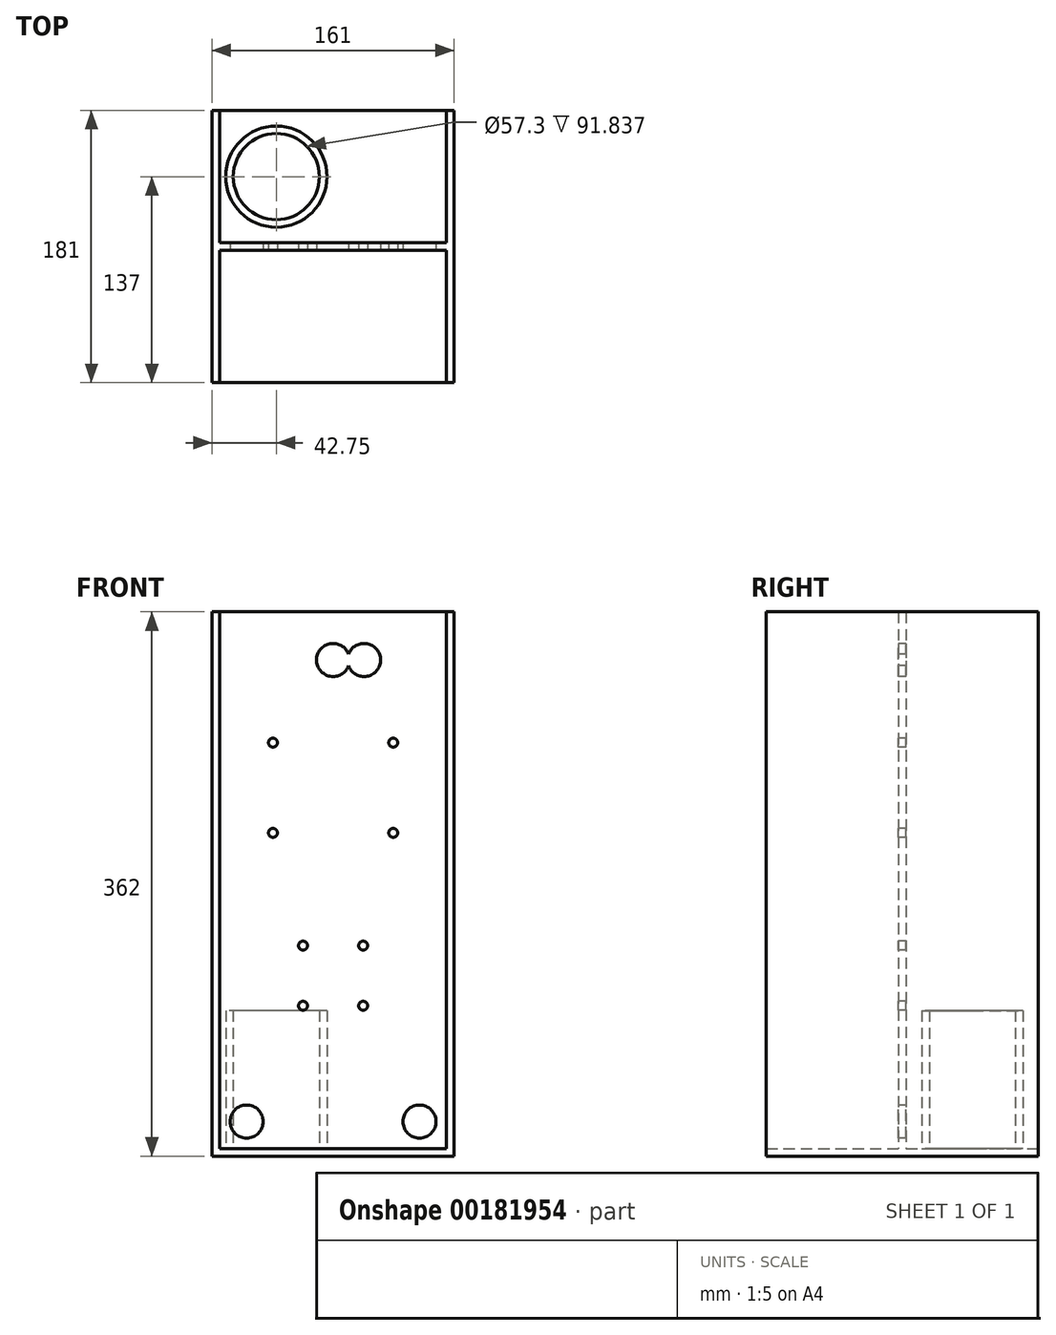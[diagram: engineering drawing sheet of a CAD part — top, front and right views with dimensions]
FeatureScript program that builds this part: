
annotation { "Feature Type Name" : "Feature", "Feature Type Description" : "" }
export const myFeature = defineFeature(function(context is Context, id is Id, definition is map)
    precondition{}
    {
        {
            var Q0;
            Q0=qCreatedBy(makeId("Top.planeOp"),FACE);
            var sketch = newSketch(context, id + "F0", { "sketchPlane" : qUnion([Q0])});
            skLineSegment(sketch, "E0.bottom", {"start": v(80.5, -90.5) * mm, "end": v(-80.5, -90.5) * mm});
            skLineSegment(sketch, "E0.top", {"start": v(80.5, 90.5) * mm, "end": v(-80.5, 90.5) * mm});
            skLineSegment(sketch, "E0.left", {"start": v(80.5, -90.5) * mm, "end": v(80.5, 90.5) * mm});
            skLineSegment(sketch, "E0.right", {"start": v(-80.5, -90.5) * mm, "end": v(-80.5, 90.5) * mm});
            skPoint(sketch, "E0.middle", {"position": v(0, 0) * mm});
            skSolve(sketch);
        }
        {
            var Q0;
            Q0 = qSketchRegion(id + "F0", true);
            extrude(context, id + "F1", {"entities" : qUnion([Q0]), "depth" : 5 * mm});
        }
        {
            var Q0;
            Q0=makeQuery(id+"F1.opExtrude","CAP_FACE",FACE,{"disambiguationData":[OSD([sQuery(id+"F0.wireOp",EDGE,"E0.bottom"),sQuery(id+"F0.wireOp",EDGE,"E0.top"),sQuery(id+"F0.wireOp",EDGE,"E0.left"),sQuery(id+"F0.wireOp",EDGE,"E0.right")])],"isStart":false});
            var sketch = newSketch(context, id + "F2", { "sketchPlane" : qUnion([Q0])});
            skLineSegment(sketch, "E1.0", {"start": v(-80.5, -90.5) * mm, "end": v(-80.5, 90.5) * mm});
            skLineSegment(sketch, "E2.0", {"start": v(80.5, -90.5) * mm, "end": v(80.5, 90.5) * mm});
            skLineSegment(sketch, "E3.0", {"start": v(80.5, 90.5) * mm, "end": v(75.5, 90.5) * mm});
            skLineSegment(sketch, "E4.0", {"start": v(80.5, -90.5) * mm, "end": v(75.5, -90.5) * mm});
            skLineSegment(sketch, "E5.0", {"start": v(-75.5, -90.5) * mm, "end": v(-75.5, 90.5) * mm});
            skLineSegment(sketch, "E6.0", {"start": v(75.5, -90.5) * mm, "end": v(75.5, 90.5) * mm});
            skLineSegment(sketch, "E7.trimOffspring", {"start": v(-75.5, 90.5) * mm, "end": v(-80.5, 90.5) * mm});
            skLineSegment(sketch, "E8.trimOffspring", {"start": v(-75.5, -90.5) * mm, "end": v(-80.5, -90.5) * mm});
            skLineSegment(sketch, "E9.bottom", {"start": v(75.5, 2.5) * mm, "end": v(-75.5, 2.5) * mm});
            skLineSegment(sketch, "E9.top", {"start": v(75.5, -2.5) * mm, "end": v(-75.5, -2.5) * mm});
            skLineSegment(sketch, "E9.left", {"start": v(75.5, 2.5) * mm, "end": v(75.5, -2.5) * mm});
            skLineSegment(sketch, "E9.right", {"start": v(-75.5, 2.5) * mm, "end": v(-75.5, -2.5) * mm});
            skPoint(sketch, "E9.middle", {"position": v(0, 0) * mm});
            skSolve(sketch);
        }
        {
            var Q0;
            Q0 = qSketchRegion(id + "F2", true);
            extrude(context, id + "F3", {"entities" : qUnion([Q0]), "operationType" : NewBodyOperationType.ADD, "depth" : 357 * mm});
        }
        {
            var Q0;
            Q0=qCreatedBy(makeId("Front.planeOp"),FACE);
            var sketch = newSketch(context, id + "F4", { "sketchPlane" : qUnion([Q0])});
            skLineSegment(sketch, "E10.0", {"start": v(-75.5, 362) * mm, "end": v(-75.5, 5) * mm});
            skLineSegment(sketch, "E11.0", {"start": v(75.5, 362) * mm, "end": v(75.5, 5) * mm});
            skLineSegment(sketch, "E12.0", {"start": v(75.5, 5) * mm, "end": v(-75.5, 5) * mm});
            skLineSegment(sketch, "E13.0", {"start": v(57.5, 362) * mm, "end": v(57.5, 23) * mm, "construction": true});
            skLineSegment(sketch, "E13.1", {"start": v(57.5, 23) * mm, "end": v(-57.5, 23) * mm, "construction": true});
            skLineSegment(sketch, "E13.2", {"start": v(-57.5, 362) * mm, "end": v(-57.5, 23) * mm, "construction": true});
            skCircle(sketch, "E14", {"center": v(-57.5, 23) * mm, "radius": 11 * mm});
            skCircle(sketch, "E15", {"center": v(57.5, 23) * mm, "radius": 11 * mm});
            skCircle(sketch, "E16", {"center": v(0, 330) * mm, "radius": 11 * mm});
            skLineSegment(sketch, "E17", {"start": v(0, 0) * mm, "end": v(0, 330) * mm, "construction": true});
            skLineSegment(sketch, "E18.bottom", {"start": v(40, 215) * mm, "end": v(-40, 215) * mm, "construction": true});
            skLineSegment(sketch, "E18.top", {"start": v(40, 275) * mm, "end": v(-40, 275) * mm, "construction": true});
            skLineSegment(sketch, "E18.left", {"start": v(40, 215) * mm, "end": v(40, 275) * mm, "construction": true});
            skLineSegment(sketch, "E18.right", {"start": v(-40, 215) * mm, "end": v(-40, 275) * mm, "construction": true});
            skPoint(sketch, "E18.middle", {"position": v(0, 245) * mm});
            skLineSegment(sketch, "E19.bottom", {"start": v(20, 100) * mm, "end": v(-20, 100) * mm, "construction": true});
            skLineSegment(sketch, "E19.top", {"start": v(20, 140) * mm, "end": v(-20, 140) * mm, "construction": true});
            skLineSegment(sketch, "E19.left", {"start": v(20, 100) * mm, "end": v(20, 140) * mm, "construction": true});
            skLineSegment(sketch, "E19.right", {"start": v(-20, 100) * mm, "end": v(-20, 140) * mm, "construction": true});
            skPoint(sketch, "E19.middle", {"position": v(0, 120) * mm});
            skCircle(sketch, "E20", {"center": v(40, 275) * mm, "radius": 3 * mm});
            skCircle(sketch, "E21", {"center": v(-40, 275) * mm, "radius": 3 * mm});
            skCircle(sketch, "E22", {"center": v(-40, 215) * mm, "radius": 3 * mm});
            skCircle(sketch, "E23", {"center": v(40, 215) * mm, "radius": 3 * mm});
            skCircle(sketch, "E24", {"center": v(-20, 140) * mm, "radius": 3 * mm});
            skCircle(sketch, "E25", {"center": v(20, 140) * mm, "radius": 3 * mm});
            skCircle(sketch, "E26", {"center": v(-20, 100) * mm, "radius": 3 * mm});
            skCircle(sketch, "E27", {"center": v(20, 100) * mm, "radius": 3 * mm});
            skLineSegment(sketch, "E28", {"start": v(0, 330) * mm, "end": v(20.62, 330) * mm, "construction": true});
            skCircle(sketch, "E29", {"center": v(20.62, 330) * mm, "radius": 11 * mm});
            skSolve(sketch);
        }
        {
            var Q0;
            Q0 = qSketchRegion(id + "F4", true);
            extrude(context, id + "F5", {"entities" : qUnion([Q0]), "operationType" : NewBodyOperationType.REMOVE, "endBound" : BoundingType.SYMMETRIC, "oppositeDirection" : true, "depth" : 25 * mm});
        }
        {
            var Q0;
            {var subQ2=sQuery(id+"F0.wireOp",EDGE,"E0.top");Q0=makeQuery(id+"F3.boolean.opBoolean","SPLIT",FACE,{"disambiguationData":[TD([makeQuery(id+"F1.opExtrude","SWEPT_FACE",FACE,{"disambiguationData":[OSD([subQ2])]})])],"derivedFrom":makeQuery(id+"F1.opExtrude","CAP_FACE",FACE,{"disambiguationData":[OSD([sQuery(id+"F0.wireOp",EDGE,"E0.bottom"),subQ2,sQuery(id+"F0.wireOp",EDGE,"E0.left"),sQuery(id+"F0.wireOp",EDGE,"E0.right")])],"isStart":false})});}
            var sketch = newSketch(context, id + "F6", { "sketchPlane" : qUnion([Q0])});
            skLineSegment(sketch, "E30", {"start": v(-75.5, 90.5) * mm, "end": v(0, 90.5) * mm, "construction": true});
            skLineSegment(sketch, "E31", {"start": v(-75.5, 2.5) * mm, "end": v(0, 90.5) * mm, "construction": true});
            skLineSegment(sketch, "E32", {"start": v(0, 90.5) * mm, "end": v(0, 2.5) * mm, "construction": true});
            skLineSegment(sketch, "E33", {"start": v(0, 46.5) * mm, "end": v(-75.5, 46.5) * mm, "construction": true});
            skLineSegment(sketch, "E34", {"start": v(-75.5, 46.5) * mm, "end": v(-37.75, 90.5) * mm, "construction": true});
            skLineSegment(sketch, "E35", {"start": v(-37.75, 90.5) * mm, "end": v(-37.75, 2.5) * mm, "construction": true});
            skLineSegment(sketch, "E36", {"start": v(-37.75, 2.5) * mm, "end": v(-75.5, 46.5) * mm, "construction": true});
            skLineSegment(sketch, "E37", {"start": v(0, 46.5) * mm, "end": v(-37.75, 2.5) * mm, "construction": true});
            skLineSegment(sketch, "E38", {"start": v(-37.75, 90.5) * mm, "end": v(0, 46.5) * mm, "construction": true});
            skLineSegment(sketch, "E39", {"start": v(-18.88, 24.5) * mm, "end": v(-56.63, 68.5) * mm, "construction": true});
            skCircle(sketch, "E40", {"center": v(-37.75, 46.5) * mm, "radius": 28.65 * mm});
            skCircle(sketch, "E41.0", {"center": v(-37.75, 46.5) * mm, "radius": 33.65 * mm});
            skSolve(sketch);
        }
        {
            var Q0;
            Q0 = qSketchRegion(id + "F6", true);
            extrude(context, id + "F7", {"entities" : qUnion([Q0]), "operationType" : NewBodyOperationType.ADD, "depth" : 91.84 * mm});
        }
    });
